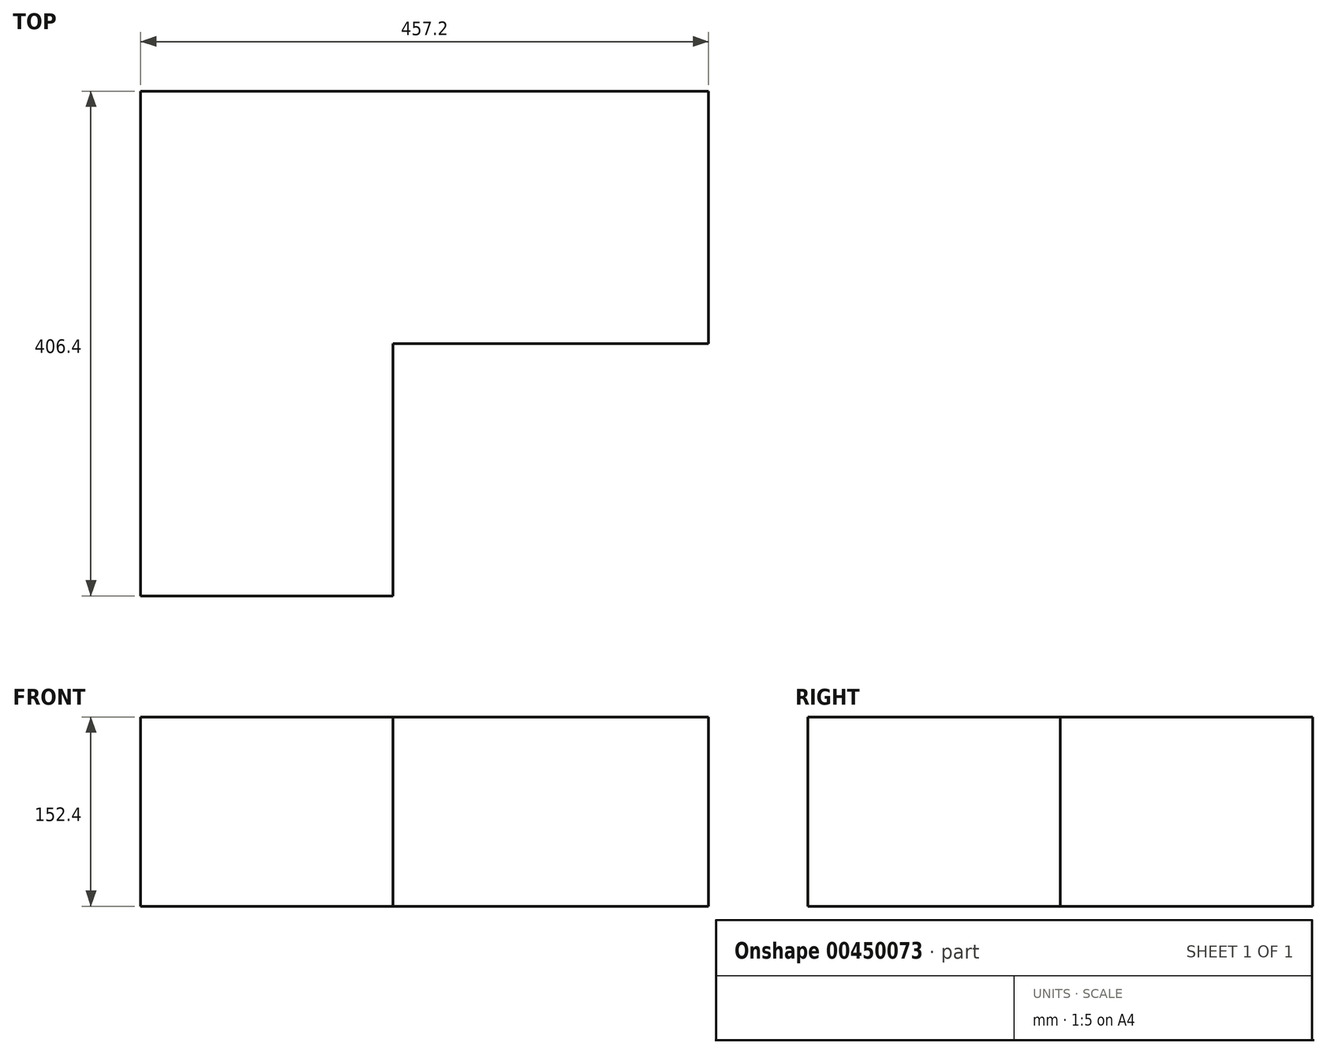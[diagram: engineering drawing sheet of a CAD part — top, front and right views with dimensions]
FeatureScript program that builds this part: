
annotation { "Feature Type Name" : "Feature", "Feature Type Description" : "" }
export const myFeature = defineFeature(function(context is Context, id is Id, definition is map)
    precondition{}
    {
        {
            var Q0;
            Q0=qCreatedBy(makeId("Top.planeOp"),FACE);
            var sketch = newSketch(context, id + "F0", { "sketchPlane" : qUnion([Q0])});
            skLineSegment(sketch, "E0.bottom", {"start": v(-228.6, 203.2) * mm, "end": v(228.6, 203.2) * mm});
            skLineSegment(sketch, "E0.top", {"start": v(-228.6, -203.2) * mm, "end": v(228.6, -203.2) * mm});
            skLineSegment(sketch, "E0.left", {"start": v(-228.6, 203.2) * mm, "end": v(-228.6, -203.2) * mm});
            skLineSegment(sketch, "E0.right", {"start": v(228.6, 203.2) * mm, "end": v(228.6, -203.2) * mm});
            skPoint(sketch, "E0.middle", {"position": v(0, 0) * mm});
            skLineSegment(sketch, "E1.bottom", {"start": v(228.6, -203.2) * mm, "end": v(-25.4, -203.2) * mm});
            skLineSegment(sketch, "E1.top", {"start": v(228.6, 0) * mm, "end": v(-25.4, 0) * mm});
            skLineSegment(sketch, "E1.left", {"start": v(228.6, -203.2) * mm, "end": v(228.6, 0) * mm});
            skLineSegment(sketch, "E1.right", {"start": v(-25.4, -203.2) * mm, "end": v(-25.4, 0) * mm});
            skSolve(sketch);
        }
        {
            var Q0;
            Q0=makeQuery(id+"F0.imprint","IMPRINT",FACE,{"disambiguationData":[TD([[makeQuery(id+"F0.imprint","IMPRINT",EDGE,{"derivedFrom":sQuery(id+"F0.wireOp",EDGE,"E0.bottom")}),-1.0]])]});
            extrude(context, id + "F1", {"entities" : qUnion([Q0]), "depth" : 152.4 * mm});
        }
    });
